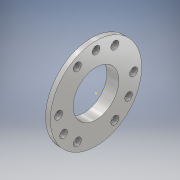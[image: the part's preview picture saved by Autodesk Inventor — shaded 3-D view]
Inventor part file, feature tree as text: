
AUTODESK INVENTOR PART (.ipt)
format: ipt  version: 2017.3 (Build 213256000, 256)  size: 151,552 bytes
history: native  units: mm
features: sketch x9, extrude x4, other x3, plane x2, hole x1
ambient origin geometry x8: Origin, YZ Plane, XZ Plane, XY Plane, X Axis, Y Axis, Z Axis, Center Point
bodies: Solid1 (feature_tree)
feature tree (19):
  extrude  "Extrusion1"  Depth=1.0mm TaperAngle=0.0deg
  sketch  "Sketch2"  dims[d3=1.0mm d4=1.67mm]
  extrude  "Extrusion2"  Depth=1.0mm
  extrude  "Extrusion3"  Depth=1.67mm
  sketch  "Sketch4"  dims[d7=1.67mm d8=1.67mm]
  other  "Work Axis1"
  other  "Work Axis2"
  plane  "Work Plane1"
  plane  "Work Plane2"
  sketch  "Sketch5"  dims[d9=1.67mm d10=12.0mm]
  other  "Work Axis3"
  sketch  "Sketch6"  dims[d11=1.5mm d12=0.0mm]
  sketch  "Sketch7"  dims[d13=1.0mm d14=0.0mm]
  hole  "Hole1"  [1 undecoded]
  extrude  "Extrusion4"  Depth=12.0mm
  sketch  "Sketch1"  dims[d0=19.0mm d1=1.0mm d2=0.0mm]
  sketch  "Sketch3"  dims[d5=1.67mm d6=1.67mm]
  sketch  "Sketch8"  dims[d15=0.0mm]
  sketch  "Sketch9"  dims[d16=1.6mm d17=3.2mm d18=4.0mm d19=2.0mm d20=90.0deg d21=1.0mm d22=0.0mm d23=9.5mm d24=3.0mm d25=0.0mm]
note: 1 required parameter value undecoded (feature->parameter linkage not recoverable at this tier; creation-order binding heuristic only, values carry confidence <= 0.55)
